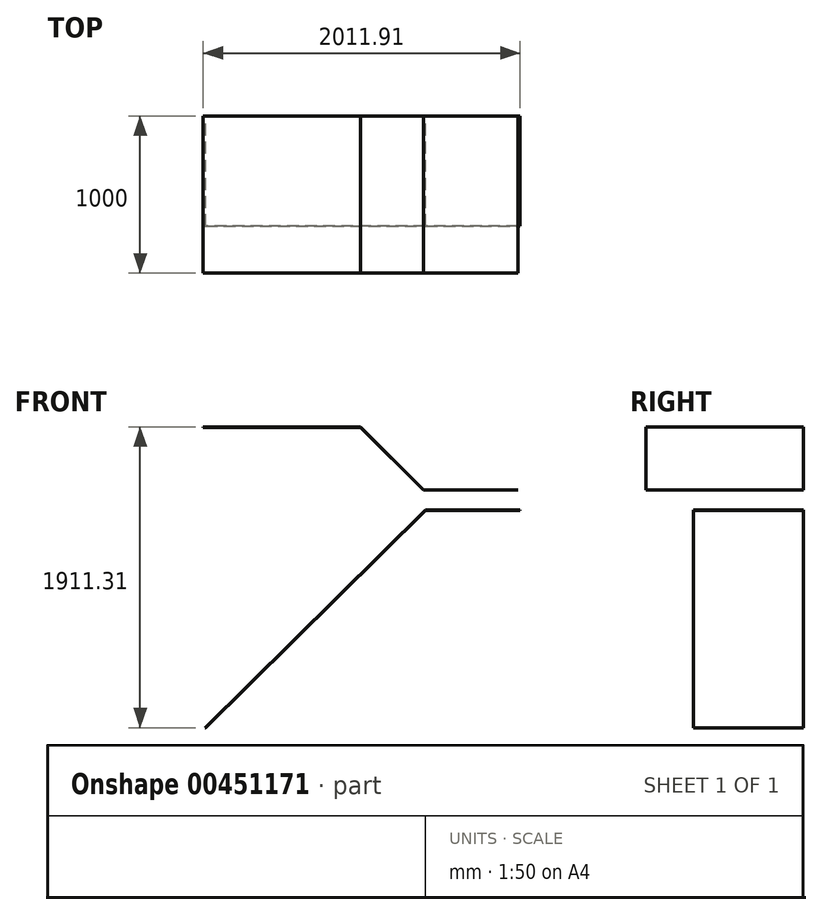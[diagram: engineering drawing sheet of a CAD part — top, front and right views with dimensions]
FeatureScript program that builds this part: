
annotation { "Feature Type Name" : "Feature", "Feature Type Description" : "" }
export const myFeature = defineFeature(function(context is Context, id is Id, definition is map)
    precondition{}
    {
        {
            var Q0;
            Q0=qCreatedBy(makeId("Front.planeOp"),FACE);
            var sketch = newSketch(context, id + "F0", { "sketchPlane" : qUnion([Q0])});
            skLineSegment(sketch, "E0.bottom", {"start": v(-1145.09, 282.85) * mm, "end": v(-145.09, 282.85) * mm});
            skLineSegment(sketch, "E0.top", {"start": v(-1145.09, 279.85) * mm, "end": v(-145.09, 279.85) * mm});
            skLineSegment(sketch, "E0.left", {"start": v(-1145.09, 282.85) * mm, "end": v(-1145.09, 279.85) * mm});
            skLineSegment(sketch, "E0.right", {"start": v(-145.09, 282.85) * mm, "end": v(-145.09, 279.85) * mm});
            skLineSegment(sketch, "E1", {"start": v(-145.09, 282.85) * mm, "end": v(254.91, -117.15) * mm});
            skLineSegment(sketch, "E2", {"start": v(254.91, -117.15) * mm, "end": v(854.91, -117.15) * mm});
            skLineSegment(sketch, "E3", {"start": v(854.91, -117.15) * mm, "end": v(854.91, -120.15) * mm});
            skLineSegment(sketch, "E4", {"start": v(854.91, -120.15) * mm, "end": v(254.91, -120.15) * mm});
            skLineSegment(sketch, "E5", {"start": v(254.91, -120.15) * mm, "end": v(-145.09, 279.85) * mm});
            skSolve(sketch);
        }
        {
            var Q0;
            Q0 = qSketchRegion(id + "F0", true);
            extrude(context, id + "F1", {"entities" : qUnion([Q0]), "depth" : 1000 * mm, "offsetDistance" : 25 * mm});
        }
        {
            var Q0;
            Q0=qCreatedBy(makeId("Front.planeOp"),FACE);
            var sketch = newSketch(context, id + "F2", { "sketchPlane" : qUnion([Q0])});
            skLineSegment(sketch, "E6", {"start": v(866.82, -245.46) * mm, "end": v(266.82, -245.46) * mm});
            skLineSegment(sketch, "E7", {"start": v(266.82, -245.46) * mm, "end": v(-1133.18, -1628.46) * mm});
            skLineSegment(sketch, "E8", {"start": v(-1133.18, -1628.46) * mm, "end": v(-1130.18, -1628.46) * mm});
            skLineSegment(sketch, "E9", {"start": v(-1130.18, -1628.46) * mm, "end": v(266.82, -248.46) * mm});
            skLineSegment(sketch, "E10", {"start": v(266.82, -248.46) * mm, "end": v(866.82, -248.46) * mm});
            skLineSegment(sketch, "E11", {"start": v(866.82, -248.46) * mm, "end": v(866.82, -245.46) * mm});
            skSolve(sketch);
        }
        {
            var Q0;
            Q0 = qSketchRegion(id + "F2", true);
            extrude(context, id + "F3", {"entities" : qUnion([Q0]), "depth" : 700 * mm, "offsetDistance" : 25 * mm});
        }
    });
